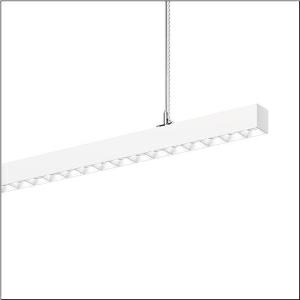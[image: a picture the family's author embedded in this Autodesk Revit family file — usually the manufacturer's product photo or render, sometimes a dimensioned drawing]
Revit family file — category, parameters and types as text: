
# Revit family: silica_r__21_51mx36da47wb_ab97
name_source: partatom
category: Lighting Fixtures
units: mm (PartAtom-declared; Revit-internal decimal feet)

## family parameters
Cut with Voids When Loaded = No
Host = Face
Light Source = No
Part Type = Normal
Room Calculation Point = No
Round Connector Dimension = Use Diameter
Shared = No

## types (1)
- --- (1 x LED, 7060 lm, 40.3 W, 4000K)
    Apparent Load = 40 VA
    CIE Flux Codes = 83 98 100 61 100
    Color Rendering = 80
    Color Temperature = 4000K
    Default Elevation = 1800 mm
    Description = Silica® 21, office luminaire, primary light control with darklight reflector, of PMMA, white, CAT 2 (L<= 3000cd/m²), light emission: direct/indirect distribution, primary light characteristic: symmetric, installation type: suspended mounting, LED, rated luminous flux: 7.060lm, luminous efficacy: 175lm/W, light colour: 840, colour temperature: 4000K, with terminal, 3+2-pole, max. 2.5mm², mains connection: 220..240V, AC, 50/60Hz, rated input power: 40.3W, luminaire housing, of aluminium, traffic white (RAL 9016), length: 1.204mm, width: 53mm, height: 53mm, protection rating (complete): IP20, insulation class (complete): insulation class I (protective earthing), certification: CE, permissible operating ambient temperature: 0..+35°C, standard: EN 50419, packaging unit: 1 piece
    Height = 53 mm
    Lamp = 1 x LED
    Lamp Light Flux = 7060 lm
    Lamp Power = 40.3 W
    Lamp count = 1
    Length = 1204 mm
    Luminous efficacy = 175 lm/W
    Manufacturer = Siteco
    ModVariant = No
    Model = 51MX36DA47WB
    Mounting Place = Ceiling
    Mounting Type = Pendant
    Number of Poles = 1
    OnlyDefault = Yes
    Power Factor = 1
    Product Name = Silica® 21
    Product group = office luminaire | ceiling pendant
    ProductGroupID = 902
    Protection Class = Protection class I
    Protection Degree = IP 20
    RLX_Detail_Level = 1
    RLX_Emergency_Light_Flux = 0 lm
    RLX_Emergency_Type = 0
    RLX_Emergency_Type_DB = No
    RlxData = <blob elided: 40617 chars, md5=32b83513>
    Socket = socket
    Standby Power = 0 W
    System Light Flux = 7060 lm
    System Power = 40 W
    Type Comments = factory setting: luminous flux: 100 % | dim-lin: 254 | 336 mA
    Type Image = l_1335921.jpg
    URL = http://relux.com
    VarID = @adj_090899
    Voltage = 0 V
    Weight = 0.00 kg
    Width = 53 mm

## geometry (parser evidence)
native form markers: Blend x4, Sweep x12
no freeform markers — native parametric forms only
